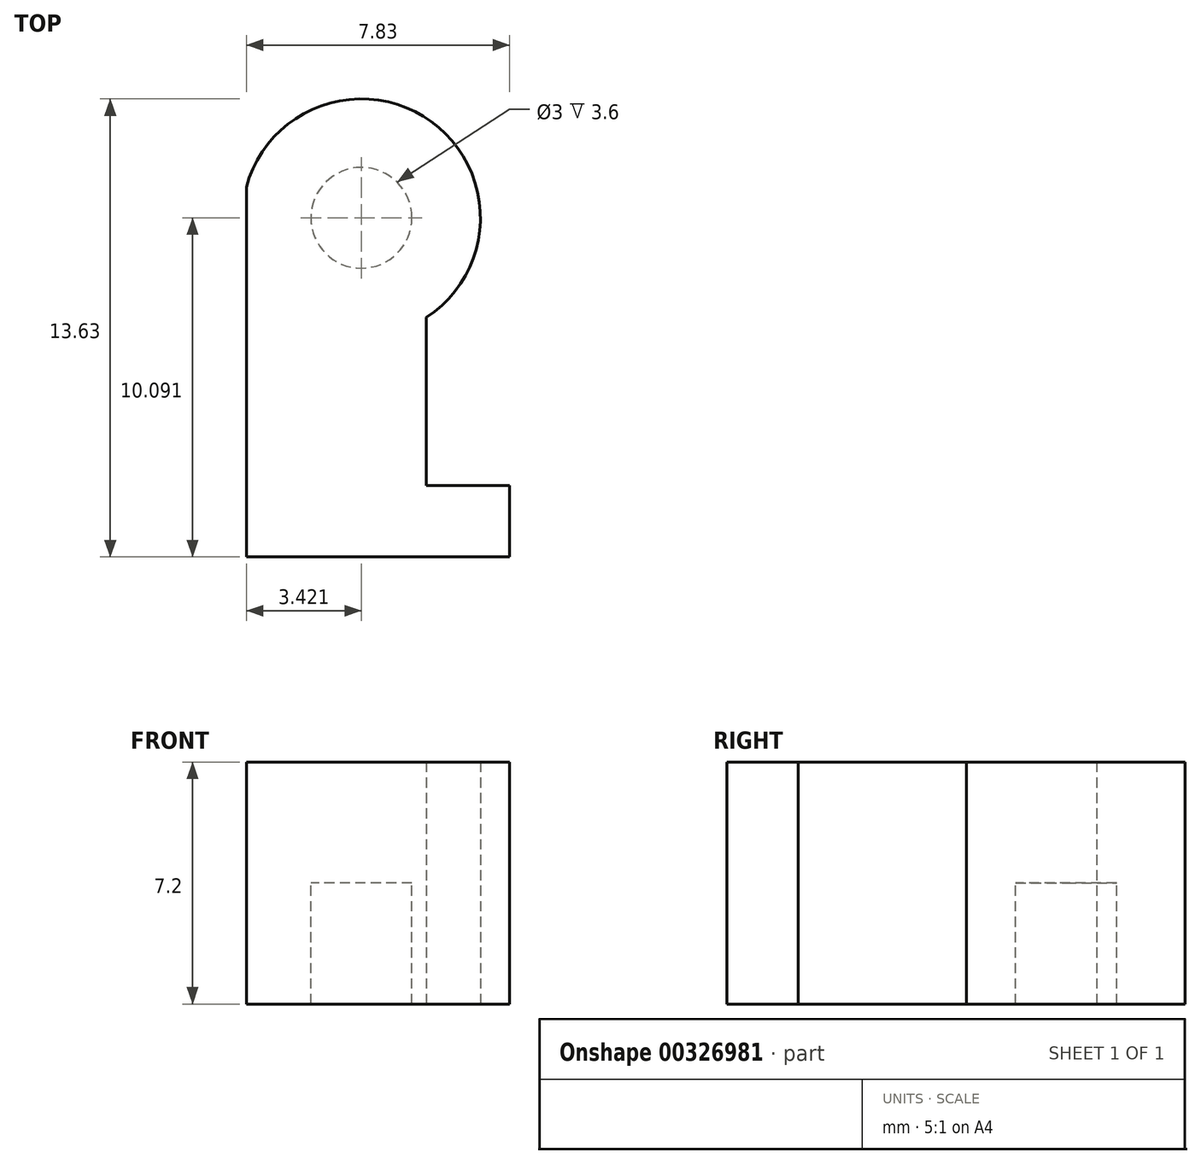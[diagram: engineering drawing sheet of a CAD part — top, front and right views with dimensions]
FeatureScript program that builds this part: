
annotation { "Feature Type Name" : "Feature", "Feature Type Description" : "" }
export const myFeature = defineFeature(function(context is Context, id is Id, definition is map)
    precondition{}
    {
        {
            var Q0;
            Q0=qCreatedBy(makeId("Top.planeOp"),FACE);
            var sketch = newSketch(context, id + "F0", { "sketchPlane" : qUnion([Q0])});
            skLineSegment(sketch, "E0", {"start": v(0, 0) * mm, "end": v(7.83, 0) * mm});
            skLineSegment(sketch, "E1", {"start": v(7.83, 0) * mm, "end": v(7.83, 2.13) * mm});
            skLineSegment(sketch, "E2", {"start": v(7.83, 2.13) * mm, "end": v(5.35, 2.13) * mm});
            skLineSegment(sketch, "E3", {"start": v(5.35, 2.13) * mm, "end": v(5.35, 7.13) * mm});
            skLineSegment(sketch, "E4", {"start": v(0, 0) * mm, "end": v(0, 11) * mm});
            skArc(sketch, "E5", {"start": v(5.35, 7.13) * mm, "mid": v(5.5, 12.96) * mm, "end": v(0, 11) * mm});
            skSolve(sketch);
        }
        {
            var Q0;
            Q0 = qSketchRegion(id + "F0", true);
            extrude(context, id + "F1", {"entities" : qUnion([Q0]), "depth" : 3.6 * mm, "hasSecondDirection" : true, "secondDirectionOppositeDirection" : true, "secondDirectionDepth" : 3.6 * mm});
        }
        {
            var Q0;
            Q0=qCreatedBy(makeId("Top.planeOp"),FACE);
            var sketch = newSketch(context, id + "F2", { "sketchPlane" : qUnion([Q0])});
            skCircle(sketch, "E6", {"center": v(3.42, 10.1) * mm, "radius": 1.5 * mm});
            skSolve(sketch);
        }
        {
            var Q0;
            Q0 = qSketchRegion(id + "F2", true);
            extrude(context, id + "F3", {"entities" : qUnion([Q0]), "operationType" : NewBodyOperationType.REMOVE, "oppositeDirection" : true, "depth" : 25 * mm});
        }
    });
